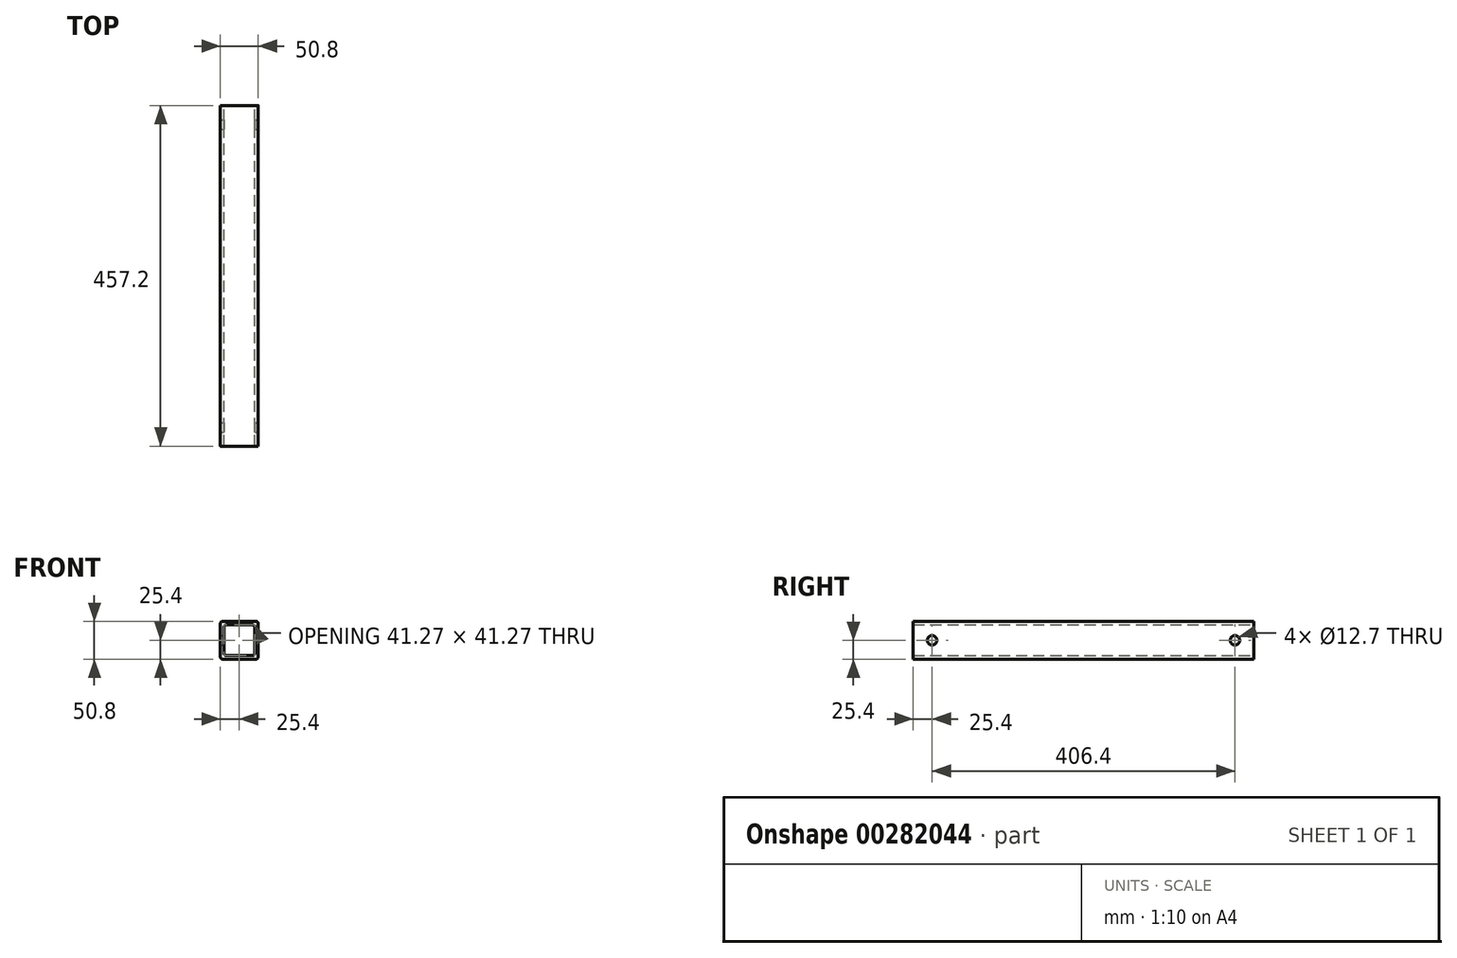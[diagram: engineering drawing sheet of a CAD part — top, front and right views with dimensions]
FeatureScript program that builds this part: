
annotation { "Feature Type Name" : "Feature", "Feature Type Description" : "" }
export const myFeature = defineFeature(function(context is Context, id is Id, definition is map)
    precondition{}
    {
        {
            var Q0;
            Q0=qCreatedBy(makeId("Front.planeOp"),FACE);
            var sketch = newSketch(context, id + "F0", { "sketchPlane" : qUnion([Q0])});
            skLineSegment(sketch, "E0.bottom", {"start": v(22.22, 25.4) * mm, "end": v(-22.22, 25.4) * mm});
            skLineSegment(sketch, "E0.top", {"start": v(22.22, -25.4) * mm, "end": v(-22.22, -25.4) * mm});
            skLineSegment(sketch, "E0.left", {"start": v(25.4, 22.22) * mm, "end": v(25.4, -22.23) * mm});
            skLineSegment(sketch, "E0.right", {"start": v(-25.4, 22.23) * mm, "end": v(-25.4, -22.22) * mm});
            skPoint(sketch, "E0.middle", {"position": v(0, 0) * mm});
            skLineSegment(sketch, "E1.bottom", {"start": v(17.46, 20.64) * mm, "end": v(-17.46, 20.64) * mm});
            skLineSegment(sketch, "E1.top", {"start": v(17.46, -20.64) * mm, "end": v(-17.46, -20.64) * mm});
            skLineSegment(sketch, "E1.left", {"start": v(20.64, 17.46) * mm, "end": v(20.64, -17.46) * mm});
            skLineSegment(sketch, "E1.right", {"start": v(-20.64, 17.46) * mm, "end": v(-20.64, -17.46) * mm});
            skPoint(sketch, "E2.visualSharp", {"position": v(-20.64, 20.64) * mm});
            skArc(sketch, "E2.filletArc", {"start": v(-17.46, 20.64) * mm, "mid": v(-19.7, 19.7) * mm, "end": v(-20.64, 17.46) * mm});
            skPoint(sketch, "E3.visualSharp", {"position": v(-25.4, 25.4) * mm});
            skArc(sketch, "E3.filletArc", {"start": v(-22.22, 25.4) * mm, "mid": v(-24.47, 24.47) * mm, "end": v(-25.4, 22.23) * mm});
            skPoint(sketch, "E4.visualSharp", {"position": v(-20.64, -20.64) * mm});
            skArc(sketch, "E4.filletArc", {"start": v(-20.64, -17.46) * mm, "mid": v(-19.7, -19.7) * mm, "end": v(-17.46, -20.64) * mm});
            skPoint(sketch, "E5.visualSharp", {"position": v(-25.4, -25.4) * mm});
            skArc(sketch, "E5.filletArc", {"start": v(-25.4, -22.22) * mm, "mid": v(-24.47, -24.47) * mm, "end": v(-22.22, -25.4) * mm});
            skPoint(sketch, "E6.visualSharp", {"position": v(20.64, -20.64) * mm});
            skArc(sketch, "E6.filletArc", {"start": v(17.46, -20.64) * mm, "mid": v(19.7, -19.7) * mm, "end": v(20.64, -17.46) * mm});
            skPoint(sketch, "E7.visualSharp", {"position": v(25.4, -25.4) * mm});
            skArc(sketch, "E7.filletArc", {"start": v(22.22, -25.4) * mm, "mid": v(24.47, -24.47) * mm, "end": v(25.4, -22.23) * mm});
            skPoint(sketch, "E8.visualSharp", {"position": v(20.64, 20.64) * mm});
            skArc(sketch, "E8.filletArc", {"start": v(20.64, 17.46) * mm, "mid": v(19.7, 19.7) * mm, "end": v(17.46, 20.64) * mm});
            skPoint(sketch, "E9.visualSharp", {"position": v(25.4, 25.4) * mm});
            skArc(sketch, "E9.filletArc", {"start": v(25.4, 22.22) * mm, "mid": v(24.47, 24.47) * mm, "end": v(22.22, 25.4) * mm});
            skSolve(sketch);
        }
        {
            var Q0;
            Q0 = qSketchRegion(id + "F0", true);
            extrude(context, id + "F1", {"entities" : qUnion([Q0]), "depth" : 457.2 * mm});
        }
        {
            var Q0;
            Q0=makeQuery(id+"F1.opExtrude","SWEPT_FACE",FACE,{"disambiguationData":[OSD([sQuery(id+"F0.wireOp",EDGE,"E0.left")])]});
            var sketch = newSketch(context, id + "F2", { "sketchPlane" : qUnion([Q0])});
            skCircle(sketch, "E10", {"center": v(-431.8, 0) * mm, "radius": 6.35 * mm});
            skCircle(sketch, "E11", {"center": v(-25.4, 0) * mm, "radius": 6.35 * mm});
            skSolve(sketch);
        }
        {
            var Q0;
            Q0 = qSketchRegion(id + "F2", true);
            extrude(context, id + "F3", {"entities" : qUnion([Q0]), "operationType" : NewBodyOperationType.REMOVE, "endBound" : BoundingType.THROUGH_ALL, "oppositeDirection" : true, "depth" : 25.4 * mm});
        }
    });
